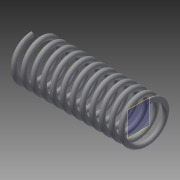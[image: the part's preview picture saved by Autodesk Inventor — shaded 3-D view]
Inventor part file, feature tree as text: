
AUTODESK INVENTOR PART (.ipt)
format: ipt  version: 2014 SP1 (Build 180222100, 222)  size: 360,960 bytes
history: native  units: in
note: dims shown in document units (in); Inventor stores cm internally (conversion verified against a paired STEP export)
features: sketch x3, extrude x2, helix x1, plane x1
ambient origin geometry x8: Origin, YZ Plane, XZ Plane, XY Plane, X Axis, Y Axis, Z Axis, Center Point
bodies: Solid1 (feature_tree)
feature tree (7):
  helix  "Coil1"  [1 undecoded]
  extrude  "Extrusion1"  Depth=1.0in TaperAngle=0.0deg
  plane  "Work Plane1"
  extrude  "Extrusion2"  Depth=1.0in TaperAngle=0.0deg
  sketch  "Sketch1"  dims[d1=0.125in]
  sketch  "Sketch2"  dims[d2=0.25in d3=1.0in d4=4.7244in d5=0.0in d6=90.0deg d7=90.0deg d8=0.0in d9=0.0in d10=1.0in d11=0.0in]
  sketch  "Sketch3"  dims[d12=-3.0in d13=1.0in d14=0.0in]
note: 1 required parameter value undecoded (feature->parameter linkage not recoverable at this tier; creation-order binding heuristic only, values carry confidence <= 0.55)
